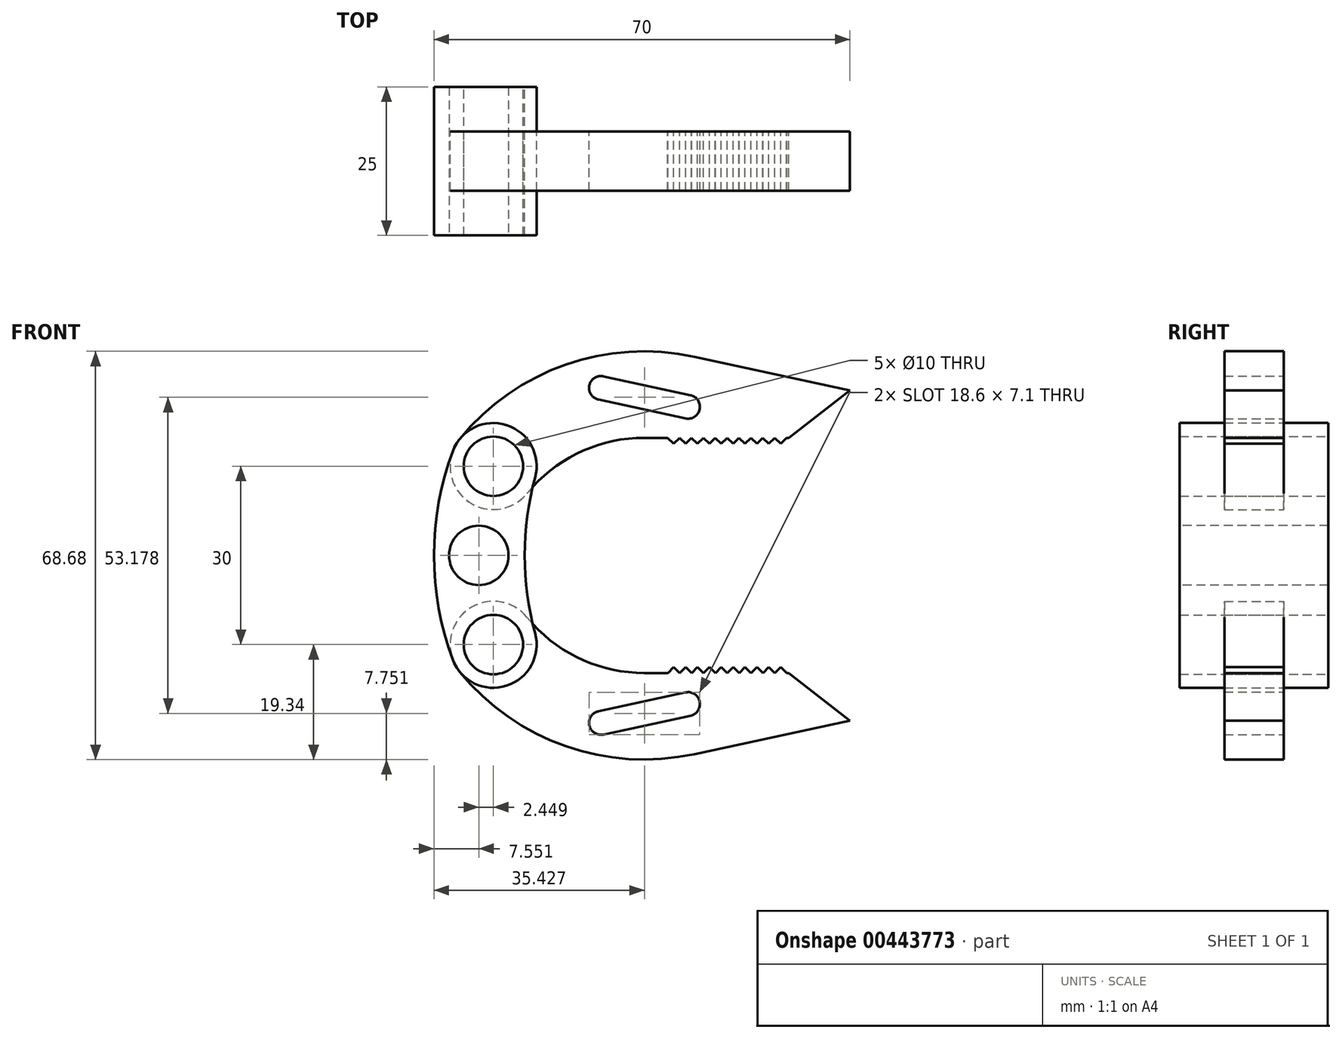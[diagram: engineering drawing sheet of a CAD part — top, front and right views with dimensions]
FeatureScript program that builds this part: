
annotation { "Feature Type Name" : "Feature", "Feature Type Description" : "" }
export const myFeature = defineFeature(function(context is Context, id is Id, definition is map)
    precondition{}
    {
        {
            var Q0;
            Q0=qCreatedBy(makeId("Front.planeOp"),FACE);
            var sketch = newSketch(context, id + "F0", { "sketchPlane" : qUnion([Q0])});
            skLineSegment(sketch, "E0", {"start": v(0, 15) * mm, "end": v(0, -15) * mm, "construction": true});
            skLineSegment(sketch, "E1", {"start": v(80, 0) * mm, "end": v(0, 0) * mm, "construction": true});
            skCircle(sketch, "E2", {"center": v(0, 15) * mm, "radius": 5 * mm});
            skCircle(sketch, "E3", {"center": v(0, -15) * mm, "radius": 5 * mm});
            skArc(sketch, "E4.0", {"start": v(-6.82, 17.56) * mm, "mid": v(2.23, 21.93) * mm, "end": v(7.03, 13.1) * mm});
            skArc(sketch, "E5.0", {"start": v(-6.82, -17.56) * mm, "mid": v(2.23, -21.93) * mm, "end": v(7.03, -13.1) * mm});
            skArc(sketch, "E6", {"start": v(7.03, 13.1) * mm, "mid": v(5.28, 0) * mm, "end": v(7.03, -13.1) * mm});
            skArc(sketch, "E7", {"start": v(-6.82, 17.56) * mm, "mid": v(-10, 0) * mm, "end": v(-6.82, -17.56) * mm});
            skSolve(sketch);
        }
        {
            var Q0;
            Q0=qCreatedBy(makeId("Front.planeOp"),FACE);
            var sketch = newSketch(context, id + "F1", { "sketchPlane" : qUnion([Q0])});
            skCircle(sketch, "E8.0", {"center": v(0, 15) * mm, "radius": 5 * mm});
            skCircle(sketch, "E9", {"center": v(0, 15) * mm, "radius": 7.28 * mm});
            skArc(sketch, "E10", {"start": v(33.82, 33.44) * mm, "mid": v(12.14, 32.09) * mm, "end": v(-5.65, 19.6) * mm});
            skLineSegment(sketch, "E11", {"start": v(33.82, 33.44) * mm, "end": v(60, 27.78) * mm});
            skLineSegment(sketch, "E12", {"start": v(60, 27.78) * mm, "end": v(49.69, 19.78) * mm});
            skLineSegment(sketch, "E13", {"start": v(49.69, 19.78) * mm, "end": v(25.37, 19.78) * mm});
            skArc(sketch, "E14", {"start": v(25.37, 19.78) * mm, "mid": v(14.45, 17.32) * mm, "end": v(5.65, 10.4) * mm});
            skLineSegment(sketch, "E15", {"start": v(33.82, 33.44) * mm, "end": v(32.76, 25) * mm, "construction": true});
            skLineSegment(sketch, "E16", {"start": v(32.76, 25) * mm, "end": v(18.1, 28.17) * mm, "construction": true});
            skArc(sketch, "E17", {"start": v(18.52, 30.13) * mm, "mid": v(16.14, 28.6) * mm, "end": v(17.67, 26.22) * mm});
            skArc(sketch, "E18", {"start": v(32.34, 23.05) * mm, "mid": v(34.73, 24.67) * mm, "end": v(33, 26.99) * mm});
            skLineSegment(sketch, "E19", {"start": v(18.52, 30.13) * mm, "end": v(33.18, 26.96) * mm});
            skLineSegment(sketch, "E20", {"start": v(17.67, 26.22) * mm, "end": v(32.34, 23.05) * mm});
            skArc(sketch, "E21.MirrorCS", {"start": v(33.82, -33.44) * mm, "mid": v(12.14, -32.09) * mm, "end": v(-5.65, -19.6) * mm});
            skLineSegment(sketch, "E22.MirrorCS", {"start": v(33.82, -33.44) * mm, "end": v(60, -27.78) * mm});
            skLineSegment(sketch, "E23.MirrorCS", {"start": v(49.69, -19.78) * mm, "end": v(25.37, -19.78) * mm});
            skLineSegment(sketch, "E24.MirrorCS", {"start": v(60, -27.78) * mm, "end": v(49.69, -19.78) * mm});
            skArc(sketch, "E25.MirrorCS", {"start": v(25.37, -19.78) * mm, "mid": v(14.45, -17.32) * mm, "end": v(5.65, -10.4) * mm});
            skCircle(sketch, "E26.MirrorC", {"center": v(0, -15) * mm, "radius": 7.28 * mm});
            skCircle(sketch, "E27.MirrorC", {"center": v(0, -15) * mm, "radius": 5 * mm});
            skLineSegment(sketch, "E28", {"start": v(0, 0) * mm, "end": v(54.23, 0) * mm, "construction": true});
            skArc(sketch, "E29.MirrorCS", {"start": v(32.34, -23.05) * mm, "mid": v(34.73, -24.67) * mm, "end": v(33, -26.99) * mm});
            skLineSegment(sketch, "E30.MirrorCS", {"start": v(17.67, -26.22) * mm, "end": v(32.34, -23.05) * mm});
            skLineSegment(sketch, "E31.MirrorCS", {"start": v(18.52, -30.13) * mm, "end": v(33.18, -26.96) * mm});
            skArc(sketch, "E32.MirrorCS", {"start": v(18.52, -30.13) * mm, "mid": v(16.14, -28.6) * mm, "end": v(17.67, -26.22) * mm});
            skLineSegment(sketch, "E33", {"start": v(29.37, -19.78) * mm, "end": v(30.37, -18.78) * mm});
            skLineSegment(sketch, "E34", {"start": v(30.37, -18.78) * mm, "end": v(31.37, -19.78) * mm});
            skLineSegment(sketch, "E35.1.0.0", {"start": v(32.37, -18.78) * mm, "end": v(33.37, -19.78) * mm});
            skLineSegment(sketch, "E35.1.0.1", {"start": v(31.37, -19.78) * mm, "end": v(32.37, -18.78) * mm});
            skLineSegment(sketch, "E35.2.0.0", {"start": v(34.37, -18.78) * mm, "end": v(35.37, -19.78) * mm});
            skLineSegment(sketch, "E35.2.0.1", {"start": v(33.37, -19.78) * mm, "end": v(34.37, -18.78) * mm});
            skLineSegment(sketch, "E35.3.0.0", {"start": v(36.37, -18.78) * mm, "end": v(37.37, -19.78) * mm});
            skLineSegment(sketch, "E35.3.0.1", {"start": v(35.37, -19.78) * mm, "end": v(36.37, -18.78) * mm});
            skLineSegment(sketch, "E35.4.0.0", {"start": v(38.37, -18.78) * mm, "end": v(39.37, -19.78) * mm});
            skLineSegment(sketch, "E35.4.0.1", {"start": v(37.37, -19.78) * mm, "end": v(38.37, -18.78) * mm});
            skLineSegment(sketch, "E35.5.0.0", {"start": v(40.37, -18.78) * mm, "end": v(41.37, -19.78) * mm});
            skLineSegment(sketch, "E35.5.0.1", {"start": v(39.37, -19.78) * mm, "end": v(40.37, -18.78) * mm});
            skLineSegment(sketch, "E35.6.0.0", {"start": v(42.37, -18.78) * mm, "end": v(43.37, -19.78) * mm});
            skLineSegment(sketch, "E35.6.0.1", {"start": v(41.37, -19.78) * mm, "end": v(42.37, -18.78) * mm});
            skLineSegment(sketch, "E35.7.0.0", {"start": v(44.37, -18.78) * mm, "end": v(45.37, -19.78) * mm});
            skLineSegment(sketch, "E35.7.0.1", {"start": v(43.37, -19.78) * mm, "end": v(44.37, -18.78) * mm});
            skLineSegment(sketch, "E35.8.0.0", {"start": v(46.37, -18.78) * mm, "end": v(47.37, -19.78) * mm});
            skLineSegment(sketch, "E35.8.0.1", {"start": v(45.37, -19.78) * mm, "end": v(46.37, -18.78) * mm});
            skLineSegment(sketch, "E35.9.0.0", {"start": v(48.37, -18.78) * mm, "end": v(49.37, -19.78) * mm});
            skLineSegment(sketch, "E35.9.0.1", {"start": v(47.37, -19.78) * mm, "end": v(48.37, -18.78) * mm});
            skLineSegment(sketch, "E35.direction1", {"start": v(25.37, -19.78) * mm, "end": v(27.37, -19.78) * mm, "construction": true});
            skLineSegment(sketch, "E36.MirrorCS", {"start": v(39.35, 19.78) * mm, "end": v(40.35, 18.78) * mm});
            skLineSegment(sketch, "E37.MirrorCS", {"start": v(34.35, 18.78) * mm, "end": v(35.35, 19.78) * mm});
            skLineSegment(sketch, "E38.MirrorCS", {"start": v(38.35, 18.78) * mm, "end": v(39.35, 19.78) * mm});
            skLineSegment(sketch, "E39.MirrorCS", {"start": v(44.35, 18.78) * mm, "end": v(45.35, 19.78) * mm});
            skLineSegment(sketch, "E40.MirrorCS", {"start": v(29.35, 19.78) * mm, "end": v(30.35, 18.78) * mm});
            skLineSegment(sketch, "E41.MirrorCS", {"start": v(46.35, 18.78) * mm, "end": v(47.35, 19.78) * mm});
            skLineSegment(sketch, "E42.MirrorCS", {"start": v(31.35, 19.78) * mm, "end": v(32.35, 18.78) * mm});
            skLineSegment(sketch, "E43.MirrorCS", {"start": v(37.35, 19.78) * mm, "end": v(38.35, 18.78) * mm});
            skLineSegment(sketch, "E44.MirrorCS", {"start": v(43.35, 19.78) * mm, "end": v(44.35, 18.78) * mm});
            skLineSegment(sketch, "E45.MirrorCS", {"start": v(36.35, 18.78) * mm, "end": v(37.35, 19.78) * mm});
            skLineSegment(sketch, "E46.MirrorCS", {"start": v(41.35, 19.78) * mm, "end": v(42.35, 18.78) * mm});
            skLineSegment(sketch, "E47.MirrorCS", {"start": v(40.35, 18.78) * mm, "end": v(41.35, 19.78) * mm});
            skLineSegment(sketch, "E48.MirrorCS", {"start": v(47.35, 19.78) * mm, "end": v(48.35, 18.78) * mm});
            skLineSegment(sketch, "E49.MirrorCS", {"start": v(30.35, 18.78) * mm, "end": v(31.35, 19.78) * mm});
            skLineSegment(sketch, "E50.MirrorCS", {"start": v(45.35, 19.78) * mm, "end": v(46.35, 18.78) * mm});
            skLineSegment(sketch, "E51.MirrorCS", {"start": v(32.35, 18.78) * mm, "end": v(33.35, 19.78) * mm});
            skLineSegment(sketch, "E52.MirrorCS", {"start": v(33.35, 19.78) * mm, "end": v(34.35, 18.78) * mm});
            skLineSegment(sketch, "E53.MirrorCS", {"start": v(42.35, 18.78) * mm, "end": v(43.35, 19.78) * mm});
            skLineSegment(sketch, "E54.MirrorCS", {"start": v(48.35, 18.78) * mm, "end": v(49.35, 19.78) * mm});
            skLineSegment(sketch, "E55.MirrorCS", {"start": v(35.35, 19.78) * mm, "end": v(36.35, 18.78) * mm});
            skSolve(sketch);
        }
        {
            var Q0;
            Q0 = qSketchRegion(id + "F0", true);
            extrude(context, id + "F2", {"entities" : qUnion([Q0]), "endBound" : BoundingType.SYMMETRIC, "depth" : 25 * mm});
        }
        {
            var Q0;
            Q0 = qSketchRegion(id + "F1", true);
            extrude(context, id + "F3", {"entities" : qUnion([Q0]), "endBound" : BoundingType.SYMMETRIC, "depth" : 10 * mm});
        }
        {
            var Q0;
            Q0=makeQuery(id+"F2.opExtrude","CAP_FACE",FACE,{"disambiguationData":[OSD([sQuery(id+"F0.wireOp",EDGE,"E2"),sQuery(id+"F0.wireOp",EDGE,"E3"),sQuery(id+"F0.wireOp",EDGE,"E4.0"),sQuery(id+"F0.wireOp",EDGE,"E5.0"),sQuery(id+"F0.wireOp",EDGE,"E6"),sQuery(id+"F0.wireOp",EDGE,"E7")])],"isStart":false});
            var sketch = newSketch(context, id + "F4", { "sketchPlane" : qUnion([Q0])});
            skCircle(sketch, "E56.0", {"center": v(0, -15) * mm, "radius": 5 * mm});
            skCircle(sketch, "E57.0", {"center": v(0, 15) * mm, "radius": 5 * mm});
            skArc(sketch, "E58", {"start": v(0, 15) * mm, "mid": v(-2.45, 0) * mm, "end": v(0, -15) * mm, "construction": true});
            skCircle(sketch, "E59", {"center": v(-2.45, 0) * mm, "radius": 5 * mm});
            skSolve(sketch);
        }
        {
            var Q0;
            Q0 = qSketchRegion(id + "F4", true);
            extrude(context, id + "F5", {"entities" : qUnion([Q0]), "operationType" : NewBodyOperationType.REMOVE, "endBound" : BoundingType.THROUGH_ALL, "oppositeDirection" : true, "depth" : 25 * mm});
        }
    });
